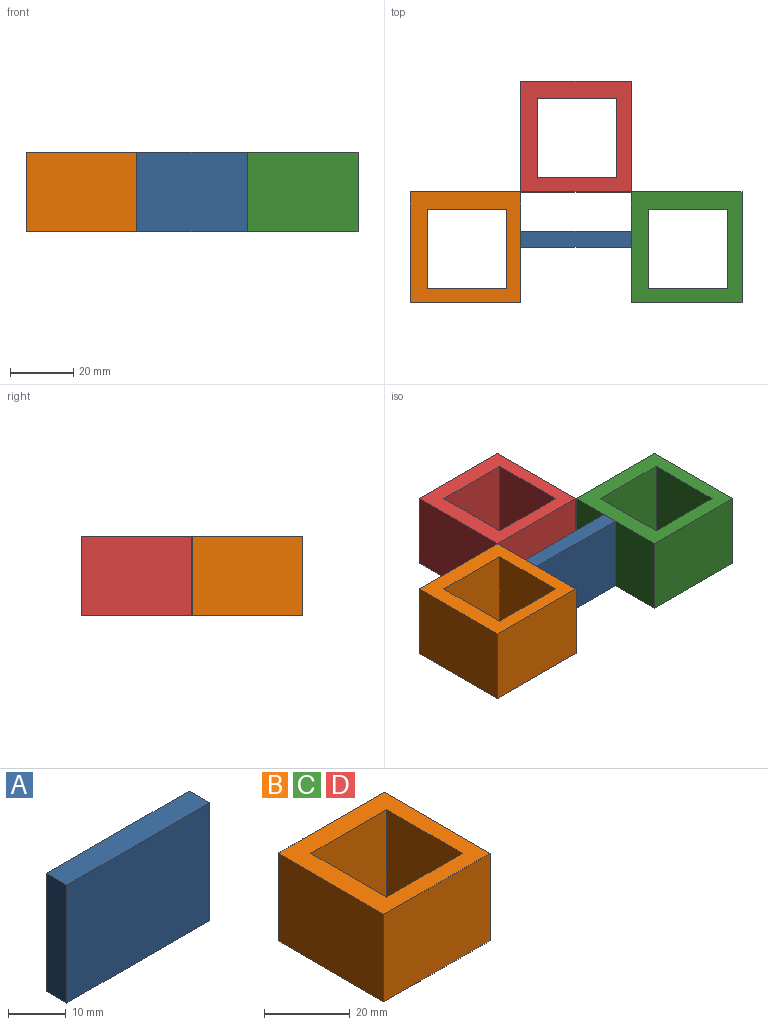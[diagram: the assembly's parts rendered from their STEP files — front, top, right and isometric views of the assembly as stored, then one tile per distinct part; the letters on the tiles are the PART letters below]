
ASSEMBLY  parts=4 mates=4
PART A: 6 faces, bbox 35x5x25 mm
  f0: plane 35x25mm, normal (0,1,0), area 875mm2, adj f1,f3,f4,f5
  f1: plane 25x5mm, normal (-1,0,0), area 125mm2, adj f0,f2,f4,f5
  f2: plane 35x25mm, normal (0,-1,0), area 875mm2, adj f1,f3,f4,f5
  f3: plane 25x5mm, normal (1,0,0), area 125mm2, adj f0,f2,f4,f5
  f4: plane 35x5mm, normal (0,0,1), area 175mm2, adj f0,f1,f2,f3
  f5: plane 35x5mm, normal (0,0,-1), area 175mm2, adj f0,f1,f2,f3
PART B: 10 faces, bbox 35x35x25 mm
  f0: plane 35x35mm, normal (0,0,1), area 600mm2, adj f2,f3,f4,f5,f6,f7,f8,f9
  f1: plane 35x35mm, normal (0,0,-1), area 600mm2, adj f2,f3,f4,f5,f6,f7,f8,f9
  f2: plane 35x25mm, normal (-1,0,0), area 875mm2, adj f0,f1,f3,f5
  f3: plane 35x25mm, normal (0,-1,0), area 875mm2, adj f0,f1,f2,f4
  f4: plane 35x25mm, normal (1,0,0), area 875mm2, adj f0,f1,f3,f5
  f5: plane 35x25mm, normal (0,1,0), area 875mm2, adj f0,f1,f2,f4
  f6: plane 25x25mm, normal (0,-1,0), area 625mm2, adj f0,f1,f7,f9
  f7: plane 25x25mm, normal (1,0,0), area 625mm2, adj f0,f1,f6,f8
  f8: plane 25x25mm, normal (0,1,0), area 625mm2, adj f0,f1,f7,f9
  f9: plane 25x25mm, normal (-1,0,0), area 625mm2, adj f0,f1,f6,f8
PART C: same geometry as B
PART D: same geometry as B
PLACE A t=(32.65,-26.45,25.56)mm
PLACE B t=(-41.8,-58.46,25.56)mm
PLACE C t=(28.2,-58.46,25.56)mm
PLACE D t=(-6.8,-23.46,25.56)mm
MATE fastened C.f0 <-> C.f0  axis (0,0,1) through (55.31,9.5,50.56)mm
MATE fastened B.f0 <-> D.f0  axis (0,0,1) through (-14.69,9.5,50.56)mm
MATE fastened C.f0 <-> D.f0  axis (0,0,1) through (20.31,9.5,50.56)mm
MATE fastened A.f1 <-> B.f4  axis (1,0,0) through (-14.69,-8,50.56)mm
